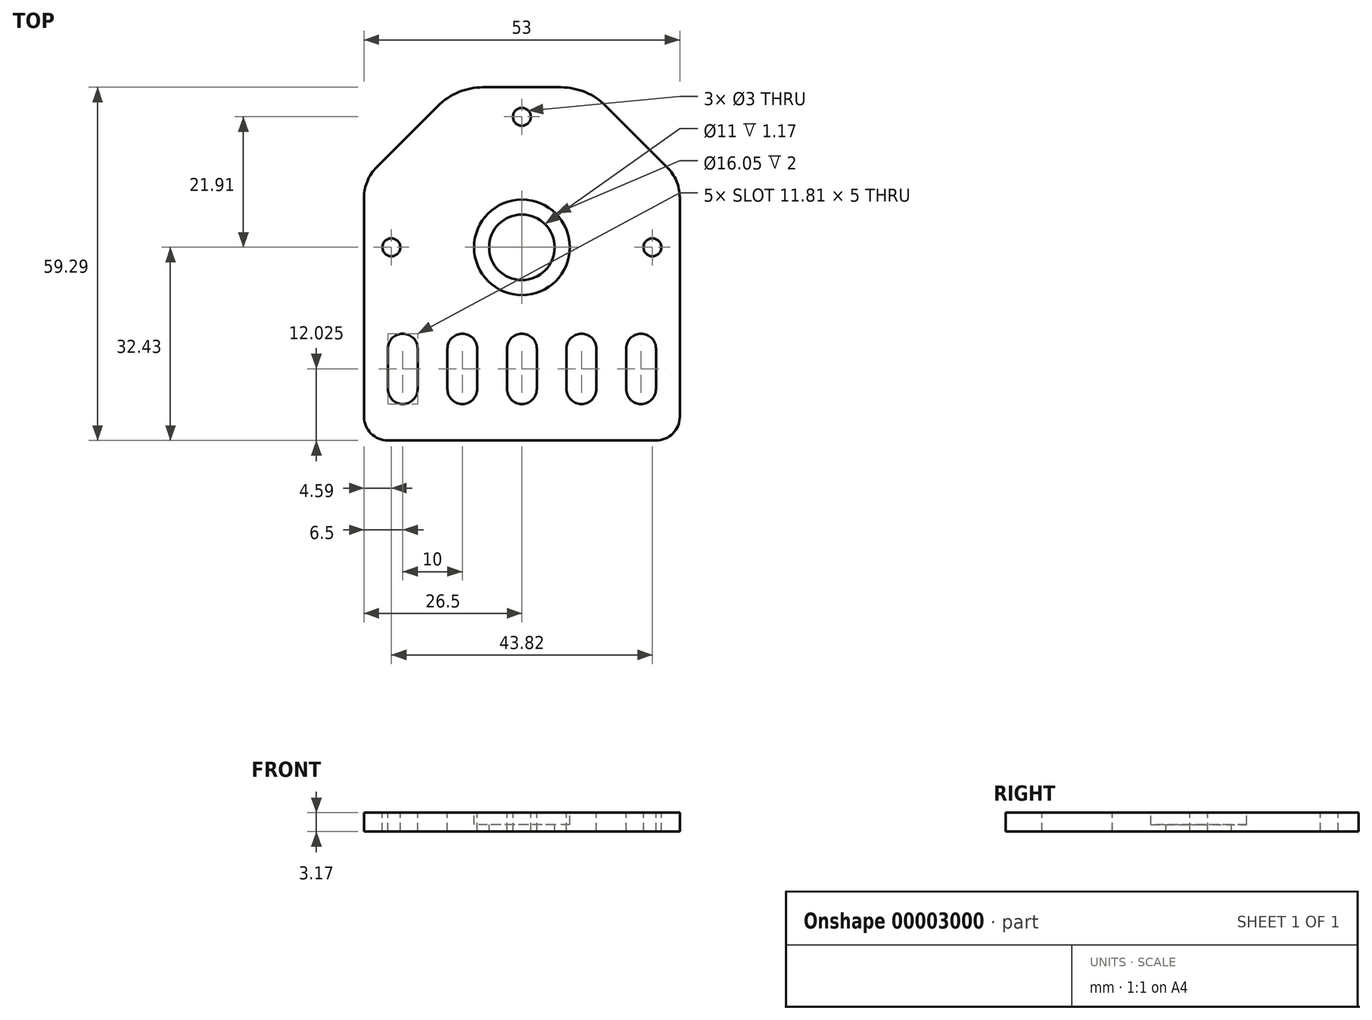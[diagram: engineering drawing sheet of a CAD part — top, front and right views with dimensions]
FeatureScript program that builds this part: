
annotation { "Feature Type Name" : "Feature", "Feature Type Description" : "" }
export const myFeature = defineFeature(function(context is Context, id is Id, definition is map)
    precondition{}
    {
        {
            var Q0;
            Q0=qCreatedBy(makeId("Top.planeOp"),FACE);
            var sketch = newSketch(context, id + "F0", { "sketchPlane" : qUnion([Q0])});
            skCircle(sketch, "E0", {"center": v(0, 0) * mm, "radius": 5.5 * mm});
            skLineSegment(sketch, "E1", {"start": v(-26.5, -32.43) * mm, "end": v(26.5, -32.43) * mm});
            skLineSegment(sketch, "E2", {"start": v(26.5, -32.43) * mm, "end": v(26.5, 11.34) * mm});
            skLineSegment(sketch, "E3", {"start": v(10.98, 26.86) * mm, "end": v(26.5, 11.34) * mm});
            skLineSegment(sketch, "E4", {"start": v(10.98, 26.86) * mm, "end": v(-10.98, 26.86) * mm});
            skLineSegment(sketch, "E5", {"start": v(-10.98, 26.86) * mm, "end": v(-26.5, 11.34) * mm});
            skLineSegment(sketch, "E6", {"start": v(-26.5, 11.34) * mm, "end": v(-26.5, -32.43) * mm});
            skPoint(sketch, "E7", {"position": v(0, 26.86) * mm});
            skPoint(sketch, "E8", {"position": v(0, -32.43) * mm});
            skCircle(sketch, "E9", {"center": v(0, 0) * mm, "radius": 21.91 * mm, "construction": true});
            skCircle(sketch, "E10", {"center": v(-21.91, 0) * mm, "radius": 1.5 * mm});
            skCircle(sketch, "E11", {"center": v(0, 21.91) * mm, "radius": 1.5 * mm});
            skCircle(sketch, "E12", {"center": v(21.91, 0) * mm, "radius": 1.5 * mm});
            skLineSegment(sketch, "E13.rect.bottom", {"start": v(2.5, -17) * mm, "end": v(-2.5, -17) * mm});
            skLineSegment(sketch, "E13.rect.top", {"start": v(2.5, -23.81) * mm, "end": v(-2.5, -23.81) * mm});
            skLineSegment(sketch, "E13.rect.left", {"start": v(2.5, -17) * mm, "end": v(2.5, -23.81) * mm});
            skLineSegment(sketch, "E13.rect.right", {"start": v(-2.5, -17) * mm, "end": v(-2.5, -23.81) * mm});
            skPoint(sketch, "E13.rect.middle", {"position": v(0, -20.4) * mm});
            skLineSegment(sketch, "E14.rect.bottom", {"start": v(7.5, -17) * mm, "end": v(12.5, -17) * mm});
            skLineSegment(sketch, "E14.rect.top", {"start": v(7.5, -23.81) * mm, "end": v(12.5, -23.81) * mm});
            skLineSegment(sketch, "E14.rect.left", {"start": v(7.5, -17) * mm, "end": v(7.5, -23.81) * mm});
            skLineSegment(sketch, "E14.rect.right", {"start": v(12.5, -17) * mm, "end": v(12.5, -23.81) * mm});
            skPoint(sketch, "E14.rect.middle", {"position": v(10, -20.4) * mm});
            skLineSegment(sketch, "E15.rect.bottom", {"start": v(17.5, -17) * mm, "end": v(22.5, -17) * mm});
            skLineSegment(sketch, "E15.rect.top", {"start": v(17.5, -23.81) * mm, "end": v(22.5, -23.81) * mm});
            skLineSegment(sketch, "E15.rect.left", {"start": v(17.5, -17) * mm, "end": v(17.5, -23.81) * mm});
            skLineSegment(sketch, "E15.rect.right", {"start": v(22.5, -17) * mm, "end": v(22.5, -23.81) * mm});
            skPoint(sketch, "E15.rect.middle", {"position": v(20, -20.4) * mm});
            skLineSegment(sketch, "E16.rect.bottom", {"start": v(-7.5, -17) * mm, "end": v(-12.5, -17) * mm});
            skLineSegment(sketch, "E16.rect.top", {"start": v(-7.5, -23.81) * mm, "end": v(-12.5, -23.81) * mm});
            skLineSegment(sketch, "E16.rect.left", {"start": v(-7.5, -17) * mm, "end": v(-7.5, -23.81) * mm});
            skLineSegment(sketch, "E16.rect.right", {"start": v(-12.5, -17) * mm, "end": v(-12.5, -23.81) * mm});
            skPoint(sketch, "E16.rect.middle", {"position": v(-10, -20.4) * mm});
            skLineSegment(sketch, "E17.rect.bottom", {"start": v(-17.5, -17) * mm, "end": v(-22.5, -17) * mm});
            skLineSegment(sketch, "E17.rect.top", {"start": v(-17.5, -23.81) * mm, "end": v(-22.5, -23.81) * mm});
            skLineSegment(sketch, "E17.rect.left", {"start": v(-17.5, -17) * mm, "end": v(-17.5, -23.81) * mm});
            skLineSegment(sketch, "E17.rect.right", {"start": v(-22.5, -17) * mm, "end": v(-22.5, -23.81) * mm});
            skPoint(sketch, "E17.rect.middle", {"position": v(-20, -20.4) * mm});
            skLineSegment(sketch, "E18", {"start": v(-20, -20.4) * mm, "end": v(-10, -20.4) * mm, "construction": true});
            skLineSegment(sketch, "E19", {"start": v(0, -20.4) * mm, "end": v(10, -20.4) * mm, "construction": true});
            skLineSegment(sketch, "E20", {"start": v(20, -20.4) * mm, "end": v(10, -20.4) * mm, "construction": true});
            skLineSegment(sketch, "E21", {"start": v(0, -20.4) * mm, "end": v(-10, -20.4) * mm, "construction": true});
            skCircle(sketch, "E22", {"center": v(-20, -17) * mm, "radius": 2.5 * mm});
            skCircle(sketch, "E23", {"center": v(-10, -17) * mm, "radius": 2.5 * mm});
            skCircle(sketch, "E24", {"center": v(0, -17) * mm, "radius": 2.5 * mm});
            skCircle(sketch, "E25", {"center": v(10, -17) * mm, "radius": 2.5 * mm});
            skCircle(sketch, "E26", {"center": v(20, -17) * mm, "radius": 2.5 * mm});
            skCircle(sketch, "E27", {"center": v(-20, -23.81) * mm, "radius": 2.5 * mm});
            skCircle(sketch, "E28", {"center": v(-10, -23.81) * mm, "radius": 2.5 * mm});
            skCircle(sketch, "E29", {"center": v(0, -23.81) * mm, "radius": 2.5 * mm});
            skCircle(sketch, "E30", {"center": v(10, -23.81) * mm, "radius": 2.5 * mm});
            skCircle(sketch, "E31", {"center": v(20, -23.81) * mm, "radius": 2.5 * mm});
            skSolve(sketch);
        }
        {
            var Q0;
            Q0 = qSketchRegion(id + "F0", true);
            var Q1;
            Q1=makeQuery(id+"F0.imprint","IMPRINT",FACE,{"disambiguationData":[TD([[makeQuery(id+"F0.imprint","IMPRINT",EDGE,{"derivedFrom":sQuery(id+"F0.wireOp",EDGE,"E0")}),-1.0]])]});
            extrude(context, id + "F1", {"entities" : qUnion([Q0, Q1]), "oppositeDirection" : true, "depth" : 3.17 * mm});
        }
        {
            var Q0;
            Q0=makeQuery(id+"F1.opExtrude","CAP_FACE",FACE,{"disambiguationData":[OSD([sQuery(id+"F0.wireOp",EDGE,"E0"),sQuery(id+"F0.wireOp",EDGE,"E1"),sQuery(id+"F0.wireOp",EDGE,"E2"),sQuery(id+"F0.wireOp",EDGE,"E3"),sQuery(id+"F0.wireOp",EDGE,"E4"),sQuery(id+"F0.wireOp",EDGE,"E5"),sQuery(id+"F0.wireOp",EDGE,"E6"),sQuery(id+"F0.wireOp",EDGE,"E10"),sQuery(id+"F0.wireOp",EDGE,"E11"),sQuery(id+"F0.wireOp",EDGE,"E12"),sQuery(id+"F0.wireOp",EDGE,"e2e10685-7645-45fd-ad4b-af4824de32fc"),sQuery(id+"F0.wireOp",EDGE,"e3a5cabc-e7d7-4b0f-ae0a-3f9be0973728"),sQuery(id+"F0.wireOp",EDGE,"e9f8da46-bf0e-437d-9901-8118a0e47073"),sQuery(id+"F0.wireOp",EDGE,"a73dd5bf-f87b-4b18-ac15-f1a73e21aadf"),sQuery(id+"F0.wireOp",EDGE,"2cfa180e-515d-4801-ac30-f05395568ccf"),sQuery(id+"F0.wireOp",EDGE,"87bfbac5-f5cb-4de0-afca-243f24f433cb"),sQuery(id+"F0.wireOp",EDGE,"8eaa9024-aab7-4628-a74b-a8dde089fb60"),sQuery(id+"F0.wireOp",EDGE,"eb0c80de-608a-4f8f-a8d6-0d99d2a70496"),sQuery(id+"F0.wireOp",EDGE,"c278f204-dcdc-4fa4-9fca-67eb5f84afdb"),sQuery(id+"F0.wireOp",EDGE,"131fdac6-95e1-431e-9b98-40ae27288e69"),sQuery(id+"F0.wireOp",EDGE,"efc9efc3-729f-4ecb-a9b4-9423b62324e3.left"),sQuery(id+"F0.wireOp",EDGE,"efc9efc3-729f-4ecb-a9b4-9423b62324e3.right"),sQuery(id+"F0.wireOp",EDGE,"84e87787-0421-438e-a34f-ecf6ee576a7b.left"),sQuery(id+"F0.wireOp",EDGE,"84e87787-0421-438e-a34f-ecf6ee576a7b.right"),sQuery(id+"F0.wireOp",EDGE,"b353f9fa-c1ab-49ed-80aa-f1ec1c134325.left"),sQuery(id+"F0.wireOp",EDGE,"b353f9fa-c1ab-49ed-80aa-f1ec1c134325.right"),sQuery(id+"F0.wireOp",EDGE,"53db4705-0393-4254-8f16-802c7a9b16b8.left"),sQuery(id+"F0.wireOp",EDGE,"53db4705-0393-4254-8f16-802c7a9b16b8.right"),sQuery(id+"F0.wireOp",EDGE,"0610733d-4043-4202-b9aa-cfad7b7ec6c5.left"),sQuery(id+"F0.wireOp",EDGE,"0610733d-4043-4202-b9aa-cfad7b7ec6c5.right")])],"isStart":true});
            var sketch = newSketch(context, id + "F2", { "sketchPlane" : qUnion([Q0])});
            skCircle(sketch, "E32", {"center": v(0, 0) * mm, "radius": 8.03 * mm});
            skSolve(sketch);
        }
        {
            var Q0;
            Q0 = qSketchRegion(id + "F2", true);
            extrude(context, id + "F3", {"entities" : qUnion([Q0]), "operationType" : NewBodyOperationType.REMOVE, "oppositeDirection" : true, "depth" : 2 * mm});
        }
        {
            var Q0;
            Q0=makeQuery(id+"F1.opExtrude","SWEPT_EDGE",EDGE,{"disambiguationData":[OSD([sQuery(id+"F0.wireOp",EDGE,"E1"),sQuery(id+"F0.wireOp",EDGE,"E6")])]});
            var Q1;
            Q1=makeQuery(id+"F1.opExtrude","SWEPT_EDGE",EDGE,{"disambiguationData":[OSD([sQuery(id+"F0.wireOp",EDGE,"E1"),sQuery(id+"F0.wireOp",EDGE,"E2")])]});
            fillet(context, id + "F4", {"entities" : qUnion([Q0, Q1]), "radius" : 4 * mm, "tangentPropagation" : true, "allowEdgeOverflow" : false});
        }
        {
            var Q0;
            Q0=makeQuery(id+"F1.opExtrude","SWEPT_EDGE",EDGE,{"disambiguationData":[OSD([sQuery(id+"F0.wireOp",EDGE,"E4"),sQuery(id+"F0.wireOp",EDGE,"E5")])]});
            var Q1;
            Q1=makeQuery(id+"F1.opExtrude","SWEPT_EDGE",EDGE,{"disambiguationData":[OSD([sQuery(id+"F0.wireOp",EDGE,"E3"),sQuery(id+"F0.wireOp",EDGE,"E4")])]});
            fillet(context, id + "F5", {"entities" : qUnion([Q0, Q1]), "radius" : 10.68 * mm, "tangentPropagation" : true, "allowEdgeOverflow" : false});
        }
        {
            var Q0;
            Q0=makeQuery(id+"F1.opExtrude","SWEPT_EDGE",EDGE,{"disambiguationData":[OSD([sQuery(id+"F0.wireOp",EDGE,"E5"),sQuery(id+"F0.wireOp",EDGE,"E6")])]});
            var Q1;
            Q1=makeQuery(id+"F1.opExtrude","SWEPT_EDGE",EDGE,{"disambiguationData":[OSD([sQuery(id+"F0.wireOp",EDGE,"E2"),sQuery(id+"F0.wireOp",EDGE,"E3")])]});
            fillet(context, id + "F6", {"entities" : qUnion([Q0, Q1]), "radius" : 7.25 * mm, "tangentPropagation" : true, "allowEdgeOverflow" : false});
        }
    });
